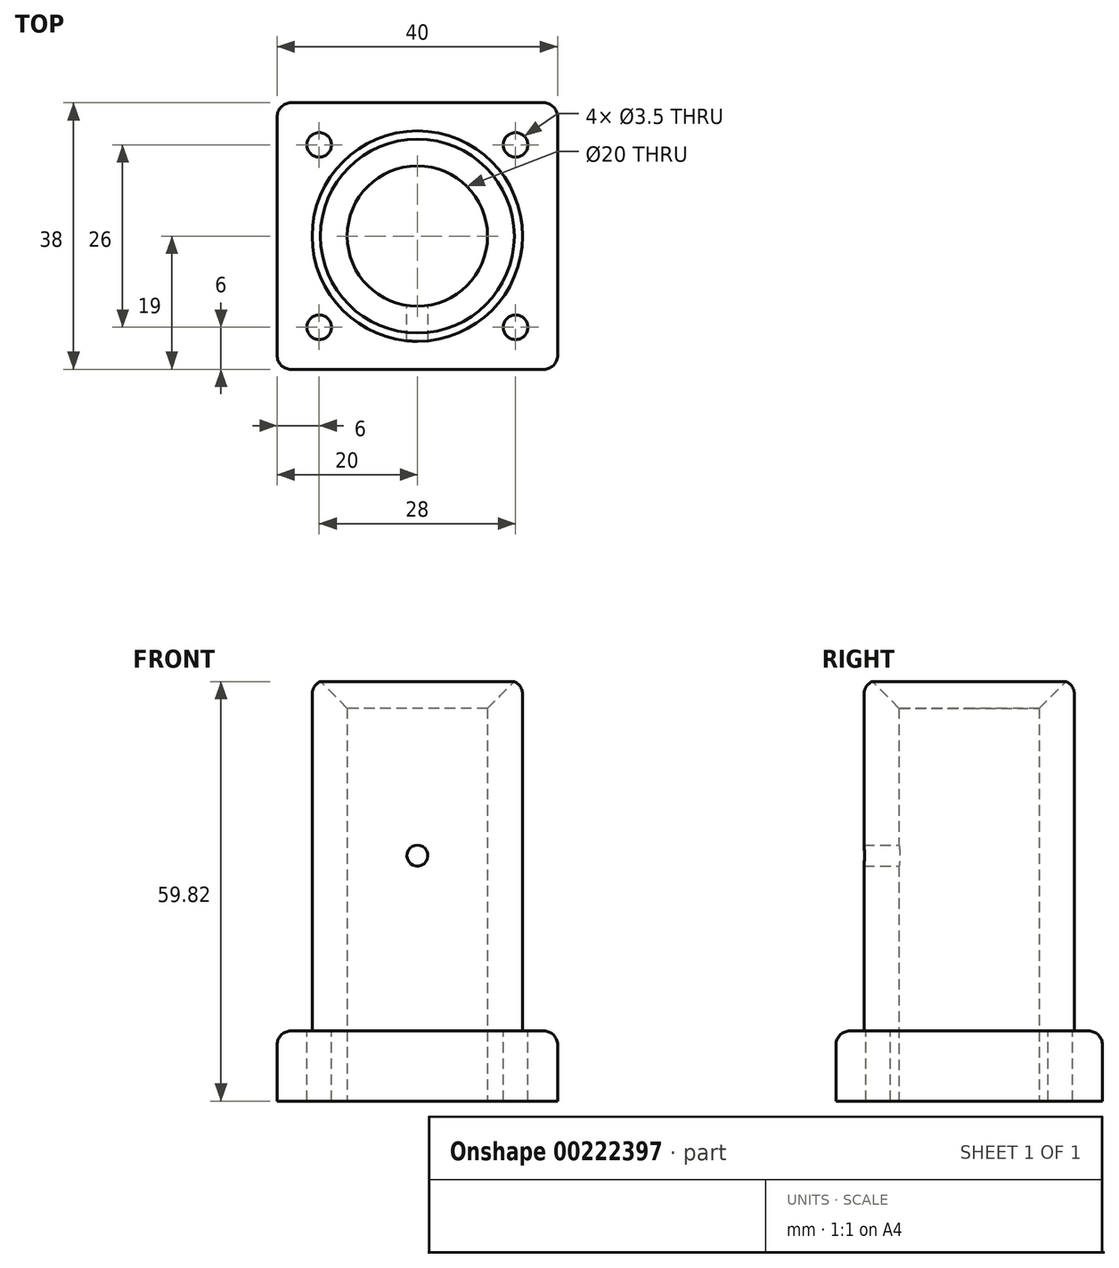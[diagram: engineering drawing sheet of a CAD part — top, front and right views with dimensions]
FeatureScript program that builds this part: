
annotation { "Feature Type Name" : "Feature", "Feature Type Description" : "" }
export const myFeature = defineFeature(function(context is Context, id is Id, definition is map)
    precondition{}
    {
        {
            var Q0;
            Q0=qCreatedBy(makeId("Top.planeOp"),FACE);
            var sketch = newSketch(context, id + "F0", { "sketchPlane" : qUnion([Q0])});
            skCircle(sketch, "E0", {"center": v(0, 0) * mm, "radius": 10 * mm});
            skLineSegment(sketch, "E1.bottom", {"start": v(20, -19) * mm, "end": v(-20, -19) * mm});
            skLineSegment(sketch, "E1.top", {"start": v(20, 19) * mm, "end": v(-20, 19) * mm});
            skLineSegment(sketch, "E1.left", {"start": v(20, -19) * mm, "end": v(20, 19) * mm});
            skLineSegment(sketch, "E1.right", {"start": v(-20, -19) * mm, "end": v(-20, 19) * mm});
            skSolve(sketch);
        }
        {
            var Q0;
            Q0 = qSketchRegion(id + "F0", true);
            extrude(context, id + "F1", {"entities" : qUnion([Q0]), "depth" : 10 * mm});
        }
        {
            var Q0;
            Q0=makeQuery(id+"F1.opExtrude","CAP_FACE",FACE,{"disambiguationData":[OSD([sQuery(id+"F0.wireOp",EDGE,"E0"),sQuery(id+"F0.wireOp",EDGE,"E1.bottom"),sQuery(id+"F0.wireOp",EDGE,"E1.top"),sQuery(id+"F0.wireOp",EDGE,"E1.left"),sQuery(id+"F0.wireOp",EDGE,"E1.right")])],"isStart":false});
            var sketch = newSketch(context, id + "F2", { "sketchPlane" : qUnion([Q0])});
            skCircle(sketch, "E2", {"center": v(0, 0) * mm, "radius": 15 * mm});
            skSolve(sketch);
        }
        {
            var Q0;
            {var subQ5=makeQuery(id+"F1.opExtrude","CAP_EDGE",EDGE,{"disambiguationData":[OSD([sQuery(id+"F0.wireOp",EDGE,"E1.left")])],"isStart":false});Q0=makeQuery(id+"F2.imprint","IMPRINT",FACE,{"disambiguationData":[TD([[makeQuery(id+"F2.imprint","IMPRINT",EDGE,{"derivedFrom":subQ5}),1.0]])]});}
            var sketch = newSketch(context, id + "F3", { "sketchPlane" : qUnion([Q0])});
            skLineSegment(sketch, "E3.0", {"start": v(14, -13) * mm, "end": v(14, 13) * mm});
            skLineSegment(sketch, "E3.1", {"start": v(14, -13) * mm, "end": v(-14, -13) * mm});
            skLineSegment(sketch, "E3.2", {"start": v(-14, -13) * mm, "end": v(-14, 13) * mm});
            skLineSegment(sketch, "E3.3", {"start": v(14, 13) * mm, "end": v(-14, 13) * mm});
            skSolve(sketch);
        }
        {
            var Q0;
            Q0=sQuery(id+"F3.wireOp",VERTEX,"E3.3.end");
            var Q1;
            Q1=sQuery(id+"F3.wireOp",VERTEX,"E3.2.start");
            var Q2;
            Q2=sQuery(id+"F3.wireOp",VERTEX,"E3.1.start");
            var Q3;
            Q3=sQuery(id+"F3.wireOp",VERTEX,"E3.3.start");
            var Q4;
            Q4=makeQuery(id+"F1.opExtrude","SWEPT_BODY",BODY,{"disambiguationData":[OSD([sQuery(id+"F0.wireOp",EDGE,"E0"),sQuery(id+"F0.wireOp",EDGE,"E1.bottom"),sQuery(id+"F0.wireOp",EDGE,"E1.top"),sQuery(id+"F0.wireOp",EDGE,"E1.left"),sQuery(id+"F0.wireOp",EDGE,"E1.right")])]});
            hole(context, id + "F4", {"style" : HoleStyle.SIMPLE, "endStyle" : HoleEndStyle.THROUGH, "holeDiameter" : 3.5 * mm, "locations" : qUnion([Q0, Q1, Q2, Q3]), "scope" : qUnion([Q4]), "isTappedThrough" : true});
        }
        {
            var Q0;
            Q0=makeQuery(id+"F2.imprint","IMPRINT",FACE,{"disambiguationData":[TD([[makeQuery(id+"F2.imprint","IMPRINT",EDGE,{"derivedFrom":makeQuery(id+"F1.opExtrude","CAP_EDGE",EDGE,{"disambiguationData":[OSD([sQuery(id+"F0.wireOp",EDGE,"E0")])],"isStart":false})}),-1.0]])]});
            extrude(context, id + "F5", {"entities" : qUnion([Q0]), "operationType" : NewBodyOperationType.ADD, "depth" : 50 * mm});
        }
        {
            var Q0;
            Q0=qCreatedBy(makeId("Front.planeOp"),FACE);
            var sketch = newSketch(context, id + "F6", { "sketchPlane" : qUnion([Q0])});
            skCircle(sketch, "E4", {"center": v(0, 35) * mm, "radius": 1.5 * mm});
            skSolve(sketch);
        }
        {
            var Q0;
            Q0 = qSketchRegion(id + "F6", true);
            extrude(context, id + "F7", {"entities" : qUnion([Q0]), "operationType" : NewBodyOperationType.REMOVE, "depth" : 25 * mm});
        }
        {
            var Q0;
            Q0=makeQuery(id+"F5.boolean.opBoolean","SPLIT",EDGE,{"disambiguationData":[OD(1.0)],"derivedFrom":makeQuery(id+"F5.opExtrude","CAP_EDGE",EDGE,{"disambiguationData":[OSD([sQuery(id+"F2.wireOp",EDGE,"E2")])],"isStart":true})});
            var Q1;
            Q1=makeQuery(id+"F1.opExtrude","CAP_EDGE",EDGE,{"disambiguationData":[OSD([sQuery(id+"F0.wireOp",EDGE,"E1.left")])],"isStart":false});
            var Q2;
            {var subQ0=sQuery(id+"F0.wireOp",EDGE,"E1.left");var subQ1=sQuery(id+"F0.wireOp",EDGE,"E1.bottom");Q2=makeQuery(id+"F5.boolean.opBoolean","SPLIT",EDGE,{"disambiguationData":[TD([makeQuery(id+"F1.opExtrude","SWEPT_FACE",FACE,{"disambiguationData":[OSD([subQ0])]})])],"derivedFrom":makeQuery(id+"F1.opExtrude","CAP_EDGE",EDGE,{"disambiguationData":[OSD([subQ1])],"isStart":false})});}
            var Q3;
            {var subQ0=sQuery(id+"F0.wireOp",EDGE,"E1.right");var subQ1=sQuery(id+"F0.wireOp",EDGE,"E1.bottom");Q3=makeQuery(id+"F5.boolean.opBoolean","SPLIT",EDGE,{"disambiguationData":[TD([makeQuery(id+"F1.opExtrude","SWEPT_FACE",FACE,{"disambiguationData":[OSD([subQ0])]})])],"derivedFrom":makeQuery(id+"F1.opExtrude","CAP_EDGE",EDGE,{"disambiguationData":[OSD([subQ1])],"isStart":false})});}
            var Q4;
            Q4=makeQuery(id+"F1.opExtrude","CAP_EDGE",EDGE,{"disambiguationData":[OSD([sQuery(id+"F0.wireOp",EDGE,"E1.right")])],"isStart":false});
            var Q5;
            {var subQ0=sQuery(id+"F0.wireOp",EDGE,"E1.left");var subQ1=sQuery(id+"F0.wireOp",EDGE,"E1.top");Q5=makeQuery(id+"F5.boolean.opBoolean","SPLIT",EDGE,{"disambiguationData":[TD([makeQuery(id+"F1.opExtrude","SWEPT_FACE",FACE,{"disambiguationData":[OSD([subQ0])]})])],"derivedFrom":makeQuery(id+"F1.opExtrude","CAP_EDGE",EDGE,{"disambiguationData":[OSD([subQ1])],"isStart":false})});}
            var Q6;
            {var subQ0=sQuery(id+"F0.wireOp",EDGE,"E1.right");var subQ1=sQuery(id+"F0.wireOp",EDGE,"E1.top");Q6=makeQuery(id+"F5.boolean.opBoolean","SPLIT",EDGE,{"disambiguationData":[TD([makeQuery(id+"F1.opExtrude","SWEPT_FACE",FACE,{"disambiguationData":[OSD([subQ0])]})])],"derivedFrom":makeQuery(id+"F1.opExtrude","CAP_EDGE",EDGE,{"disambiguationData":[OSD([subQ1])],"isStart":false})});}
            var Q7;
            Q7=makeQuery(id+"F1.opExtrude","SWEPT_EDGE",EDGE,{"disambiguationData":[OSD([sQuery(id+"F0.wireOp",EDGE,"E1.top"),sQuery(id+"F0.wireOp",EDGE,"E1.left")])]});
            var Q8;
            Q8=makeQuery(id+"F1.opExtrude","SWEPT_EDGE",EDGE,{"disambiguationData":[OSD([sQuery(id+"F0.wireOp",EDGE,"E1.bottom"),sQuery(id+"F0.wireOp",EDGE,"E1.right")])]});
            var Q9;
            Q9=makeQuery(id+"F1.opExtrude","SWEPT_EDGE",EDGE,{"disambiguationData":[OSD([sQuery(id+"F0.wireOp",EDGE,"E1.bottom"),sQuery(id+"F0.wireOp",EDGE,"E1.left")])]});
            var Q10;
            Q10=makeQuery(id+"F5.opExtrude","CAP_EDGE",EDGE,{"disambiguationData":[OSD([sQuery(id+"F2.wireOp",EDGE,"E2")])],"isStart":false});
            var Q11;
            Q11=makeQuery(id+"F5.boolean.opBoolean","SPLIT",EDGE,{"disambiguationData":[OD(0.0)],"derivedFrom":makeQuery(id+"F5.opExtrude","CAP_EDGE",EDGE,{"disambiguationData":[OSD([sQuery(id+"F2.wireOp",EDGE,"E2")])],"isStart":true})});
            var Q12;
            Q12=makeQuery(id+"F1.opExtrude","SWEPT_EDGE",EDGE,{"disambiguationData":[OSD([sQuery(id+"F0.wireOp",EDGE,"E1.top"),sQuery(id+"F0.wireOp",EDGE,"E1.right")])]});
            fillet(context, id + "F8", {"entities" : qUnion([Q0, Q1, Q2, Q3, Q4, Q5, Q6, Q7, Q8, Q9, Q10, Q11, Q12]), "radius" : 2 * mm, "tangentPropagation" : true, "allowEdgeOverflow" : false});
        }
        {
            var Q0;
            Q0=makeQuery(id+"F5.opExtrude","CAP_EDGE",EDGE,{"disambiguationData":[OSD([sQuery(id+"F0.wireOp",EDGE,"E0")])],"isStart":false});
            chamfer(context, id + "F9", {"entities" : qUnion([Q0]), "width" : 4 * mm, "tangentPropagation" : true});
        }
    });
